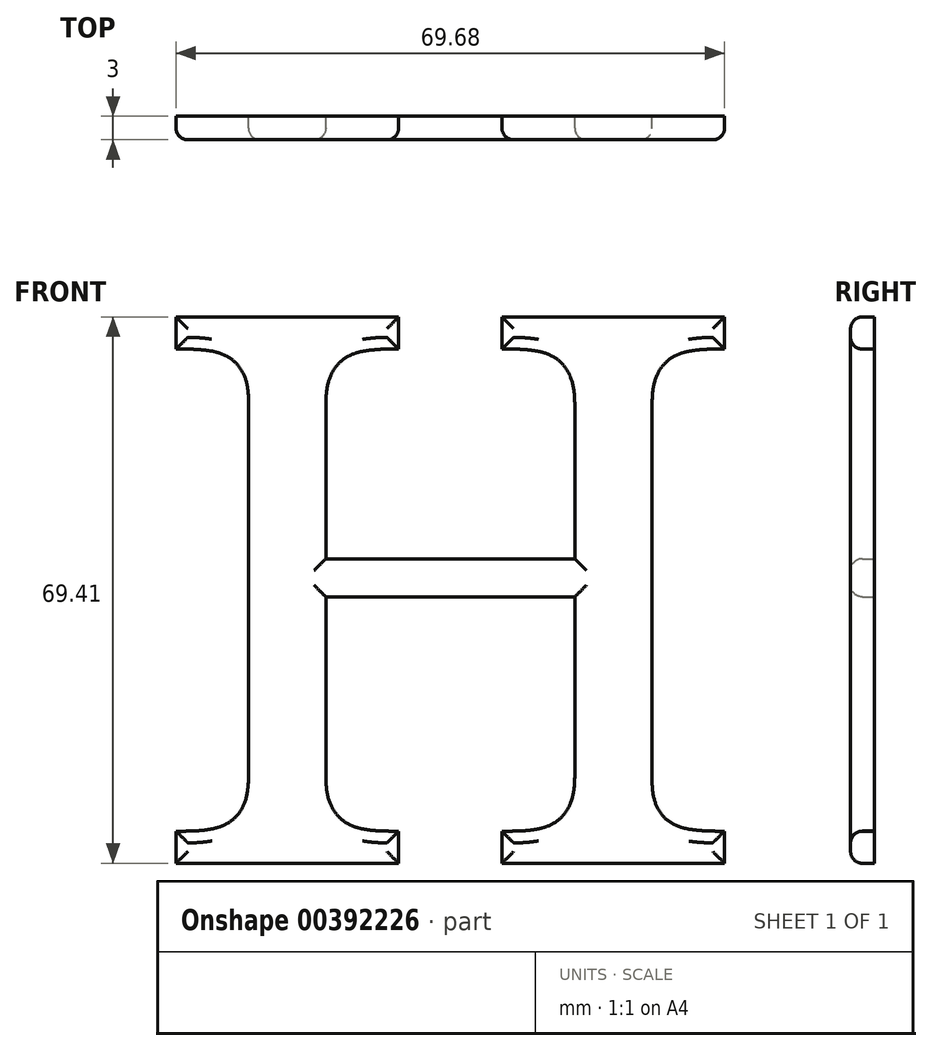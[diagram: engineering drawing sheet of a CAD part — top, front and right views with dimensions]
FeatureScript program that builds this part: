
annotation { "Feature Type Name" : "Feature", "Feature Type Description" : "" }
export const myFeature = defineFeature(function(context is Context, id is Id, definition is map)
    precondition{}
    {
        {
            var Q0;
            Q0=qCreatedBy(makeId("Front.planeOp"),FACE);
            var sketch = newSketch(context, id + "F0", { "sketchPlane" : qUnion([Q0])});
            skText(sketch, "E0", { "text": "H", "fontName": "NotoSerif-Regular.ttf"});
            const initialGuessF0  = {"E0": [0, 0, 1, 0, 0.07]};
            skSetInitialGuess(sketch, initialGuessF0);
            skSolve(sketch);
        }
        {
            var Q0;
            Q0 = qSketchRegion(id + "F0", true);
            extrude(context, id + "F1", {"entities" : qUnion([Q0]), "depth" : 3 * mm});
        }
        {
            var Q0;
            Q0=makeQuery(id+"F1.opExtrude","CAP_FACE",FACE,{"disambiguationData":[OSD([sQuery(id+"F0.wireOp",EDGE,"E0.sketch_text.stroke-0"),sQuery(id+"F0.wireOp",EDGE,"E0.sketch_text.stroke-1"),sQuery(id+"F0.wireOp",EDGE,"E0.sketch_text.stroke-2"),sQuery(id+"F0.wireOp",EDGE,"E0.sketch_text.stroke-3"),sQuery(id+"F0.wireOp",EDGE,"E0.sketch_text.stroke-4"),sQuery(id+"F0.wireOp",EDGE,"E0.sketch_text.stroke-5"),sQuery(id+"F0.wireOp",EDGE,"E0.sketch_text.stroke-6"),sQuery(id+"F0.wireOp",EDGE,"E0.sketch_text.stroke-7"),sQuery(id+"F0.wireOp",EDGE,"E0.sketch_text.stroke-8"),sQuery(id+"F0.wireOp",EDGE,"E0.sketch_text.stroke-9"),sQuery(id+"F0.wireOp",EDGE,"E0.sketch_text.stroke-10"),sQuery(id+"F0.wireOp",EDGE,"E0.sketch_text.stroke-11"),sQuery(id+"F0.wireOp",EDGE,"E0.sketch_text.stroke-12"),sQuery(id+"F0.wireOp",EDGE,"E0.sketch_text.stroke-13"),sQuery(id+"F0.wireOp",EDGE,"E0.sketch_text.stroke-14"),sQuery(id+"F0.wireOp",EDGE,"E0.sketch_text.stroke-15"),sQuery(id+"F0.wireOp",EDGE,"E0.sketch_text.stroke-16"),sQuery(id+"F0.wireOp",EDGE,"E0.sketch_text.stroke-17"),sQuery(id+"F0.wireOp",EDGE,"E0.sketch_text.stroke-18"),sQuery(id+"F0.wireOp",EDGE,"E0.sketch_text.stroke-19"),sQuery(id+"F0.wireOp",EDGE,"E0.sketch_text.stroke-20"),sQuery(id+"F0.wireOp",EDGE,"E0.sketch_text.stroke-21"),sQuery(id+"F0.wireOp",EDGE,"E0.sketch_text.stroke-22"),sQuery(id+"F0.wireOp",EDGE,"E0.sketch_text.stroke-23"),sQuery(id+"F0.wireOp",EDGE,"E0.sketch_text.stroke-24"),sQuery(id+"F0.wireOp",EDGE,"E0.sketch_text.stroke-25"),sQuery(id+"F0.wireOp",EDGE,"E0.sketch_text.stroke-26"),sQuery(id+"F0.wireOp",EDGE,"E0.sketch_text.stroke-27"),sQuery(id+"F0.wireOp",EDGE,"E0.sketch_text.stroke-28"),sQuery(id+"F0.wireOp",EDGE,"E0.sketch_text.stroke-29"),sQuery(id+"F0.wireOp",EDGE,"E0.sketch_text.stroke-30"),sQuery(id+"F0.wireOp",EDGE,"E0.sketch_text.stroke-31"),sQuery(id+"F0.wireOp",EDGE,"E0.sketch_text.stroke-32"),sQuery(id+"F0.wireOp",EDGE,"E0.sketch_text.stroke-33"),sQuery(id+"F0.wireOp",EDGE,"E0.sketch_text.stroke-34"),sQuery(id+"F0.wireOp",EDGE,"E0.sketch_text.stroke-35"),sQuery(id+"F0.wireOp",EDGE,"E0.sketch_text.stroke-36"),sQuery(id+"F0.wireOp",EDGE,"E0.sketch_text.stroke-37"),sQuery(id+"F0.wireOp",EDGE,"E0.sketch_text.stroke-38"),sQuery(id+"F0.wireOp",EDGE,"E0.sketch_text.stroke-39"),sQuery(id+"F0.wireOp",EDGE,"E0.sketch_text.stroke-40"),sQuery(id+"F0.wireOp",EDGE,"E0.sketch_text.stroke-41"),sQuery(id+"F0.wireOp",EDGE,"E0.sketch_text.stroke-42"),sQuery(id+"F0.wireOp",EDGE,"E0.sketch_text.stroke-43"),sQuery(id+"F0.wireOp",EDGE,"E0.sketch_text.stroke-44"),sQuery(id+"F0.wireOp",EDGE,"E0.sketch_text.stroke-45"),sQuery(id+"F0.wireOp",EDGE,"E0.sketch_text.stroke-46"),sQuery(id+"F0.wireOp",EDGE,"E0.sketch_text.stroke-47"),sQuery(id+"F0.wireOp",EDGE,"E0.sketch_text.stroke-48"),sQuery(id+"F0.wireOp",EDGE,"E0.sketch_text.stroke-49"),sQuery(id+"F0.wireOp",EDGE,"E0.sketch_text.stroke-50"),sQuery(id+"F0.wireOp",EDGE,"E0.sketch_text.stroke-51"),sQuery(id+"F0.wireOp",EDGE,"E0.sketch_text.stroke-52"),sQuery(id+"F0.wireOp",EDGE,"E0.sketch_text.stroke-53"),sQuery(id+"F0.wireOp",EDGE,"E0.sketch_text.stroke-54"),sQuery(id+"F0.wireOp",EDGE,"E0.sketch_text.stroke-55"),sQuery(id+"F0.wireOp",EDGE,"E0.sketch_text.stroke-56"),sQuery(id+"F0.wireOp",EDGE,"E0.sketch_text.stroke-57"),sQuery(id+"F0.wireOp",EDGE,"E0.sketch_text.stroke-58"),sQuery(id+"F0.wireOp",EDGE,"E0.sketch_text.stroke-59")])],"isStart":false});
            fillet(context, id + "F2", {"entities" : qUnion([Q0]), "radius" : 1.5 * mm, "tangentPropagation" : true, "allowEdgeOverflow" : false});
        }
    });
